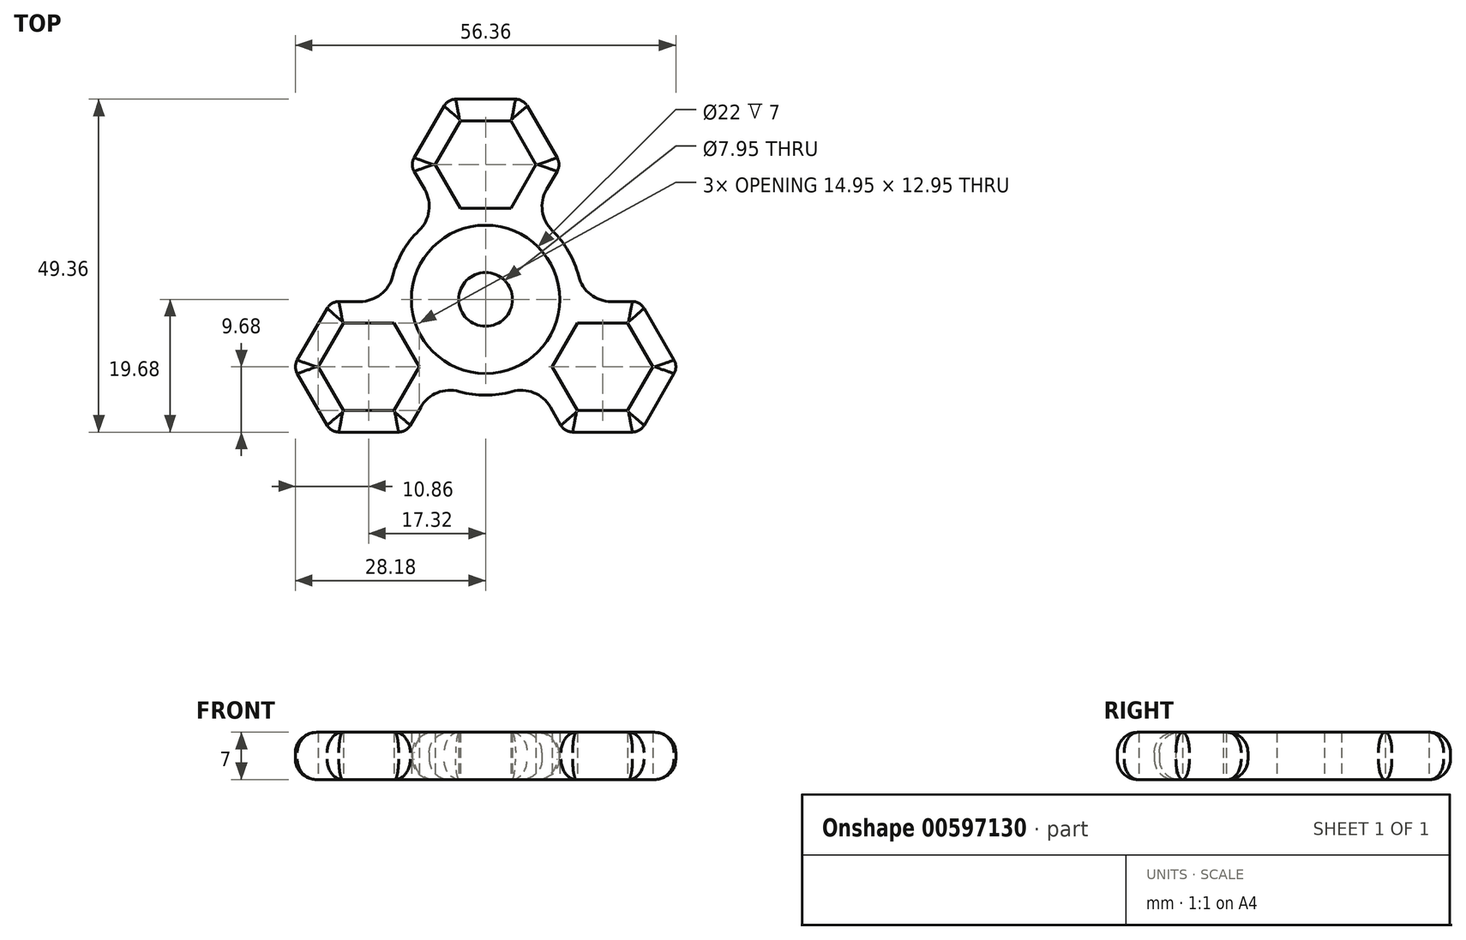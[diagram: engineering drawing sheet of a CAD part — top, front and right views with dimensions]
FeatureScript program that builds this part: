
annotation { "Feature Type Name" : "Feature", "Feature Type Description" : "" }
export const myFeature = defineFeature(function(context is Context, id is Id, definition is map)
    precondition{}
    {
        {
            var Q0;
            Q0=qCreatedBy(makeId("Top.planeOp"),FACE);
            var sketch = newSketch(context, id + "F0", { "sketchPlane" : qUnion([Q0])});
            skCircle(sketch, "E0", {"center": v(0, 0) * mm, "radius": 11 * mm});
            skCircle(sketch, "E1", {"center": v(0, 0) * mm, "radius": 3.98 * mm});
            skSolve(sketch);
        }
        {
            var Q0;
            Q0=qSketchRegion(id+"F0",true);
            extrude(context, id + "F1", {"entities" : qUnion([Q0]), "depth" : 7 * mm, "offsetDistance" : 25 * mm});
        }
        {
            var Q0;
            Q0=qCreatedBy(makeId("Top.planeOp"),FACE);
            var sketch = newSketch(context, id + "F2", { "sketchPlane" : qUnion([Q0])});
            skCircle(sketch, "E2.cCircle", {"center": v(0, 20) * mm, "radius": 6.47 * mm, "construction": true});
            skLineSegment(sketch, "E2.0", {"start": v(3.74, 26.48) * mm, "end": v(7.48, 20) * mm});
            skLineSegment(sketch, "E2.1", {"start": v(7.48, 20) * mm, "end": v(3.74, 13.53) * mm});
            skLineSegment(sketch, "E2.2", {"start": v(3.74, 13.53) * mm, "end": v(-3.74, 13.53) * mm});
            skLineSegment(sketch, "E2.3", {"start": v(-3.74, 13.52) * mm, "end": v(-7.48, 20) * mm});
            skLineSegment(sketch, "E2.4", {"start": v(-7.48, 20) * mm, "end": v(-3.74, 26.47) * mm});
            skLineSegment(sketch, "E2.5", {"start": v(-3.74, 26.47) * mm, "end": v(3.74, 26.47) * mm});
            skPoint(sketch, "E2.0.midPoint", {"position": v(5.6, 23.24) * mm});
            skLineSegment(sketch, "E3", {"start": v(0, 0) * mm, "end": v(0, 20) * mm, "construction": true});
            skLineSegment(sketch, "E4", {"start": v(0, 0) * mm, "end": v(-17.32, -10) * mm, "construction": true});
            skLineSegment(sketch, "E5", {"start": v(0, 0) * mm, "end": v(17.32, -10) * mm, "construction": true});
            skLineSegment(sketch, "E6.0", {"start": v(-4.43, 29.67) * mm, "end": v(4.43, 29.67) * mm});
            skLineSegment(sketch, "E6.1", {"start": v(10.6, 19) * mm, "end": v(9.03, 16.29) * mm});
            skLineSegment(sketch, "E6.3", {"start": v(6.16, 28.68) * mm, "end": v(10.6, 21) * mm});
            skLineSegment(sketch, "E6.4", {"start": v(-9.03, 16.29) * mm, "end": v(-10.6, 19) * mm});
            skLineSegment(sketch, "E6.5", {"start": v(-10.6, 21) * mm, "end": v(-6.16, 28.67) * mm});
            skCircle(sketch, "E7", {"center": v(0, 0) * mm, "radius": 11 * mm});
            skArc(sketch, "E8", {"start": v(-9.88, 10.2) * mm, "mid": v(-12.3, 7.1) * mm, "end": v(-13.77, 3.46) * mm});
            skLineSegment(sketch, "E9.1.0", {"start": v(-13.58, -16.47) * mm, "end": v(-21.06, -16.47) * mm});
            skLineSegment(sketch, "E9.1.1", {"start": v(-21.06, -16.48) * mm, "end": v(-24.8, -10) * mm});
            skLineSegment(sketch, "E9.1.2", {"start": v(-12.89, -19.67) * mm, "end": v(-21.75, -19.68) * mm});
            skLineSegment(sketch, "E9.1.3", {"start": v(-23.48, -18.68) * mm, "end": v(-27.91, -11) * mm});
            skLineSegment(sketch, "E9.1.4", {"start": v(-27.91, -9) * mm, "end": v(-23.48, -1.33) * mm});
            skLineSegment(sketch, "E9.1.5", {"start": v(-24.8, -10) * mm, "end": v(-21.06, -3.52) * mm});
            skLineSegment(sketch, "E9.1.6", {"start": v(-21.06, -3.53) * mm, "end": v(-13.58, -3.52) * mm});
            skLineSegment(sketch, "E9.1.7", {"start": v(-21.75, -0.33) * mm, "end": v(-18.62, -0.33) * mm});
            skLineSegment(sketch, "E9.1.8", {"start": v(-13.58, -3.52) * mm, "end": v(-9.84, -10) * mm});
            skLineSegment(sketch, "E9.1.9", {"start": v(-9.84, -10) * mm, "end": v(-13.58, -16.47) * mm});
            skLineSegment(sketch, "E9.1.10", {"start": v(-9.6, -15.96) * mm, "end": v(-11.16, -18.67) * mm});
            skLineSegment(sketch, "E9.2.0", {"start": v(21.06, -3.52) * mm, "end": v(24.8, -10) * mm});
            skLineSegment(sketch, "E9.2.1", {"start": v(24.8, -10) * mm, "end": v(21.06, -16.48) * mm});
            skLineSegment(sketch, "E9.2.2", {"start": v(23.48, -1.33) * mm, "end": v(27.91, -9) * mm});
            skLineSegment(sketch, "E9.2.3", {"start": v(27.91, -11) * mm, "end": v(23.48, -18.67) * mm});
            skLineSegment(sketch, "E9.2.4", {"start": v(21.75, -19.67) * mm, "end": v(12.89, -19.67) * mm});
            skLineSegment(sketch, "E9.2.5", {"start": v(21.06, -16.48) * mm, "end": v(13.58, -16.48) * mm});
            skLineSegment(sketch, "E9.2.6", {"start": v(13.58, -16.48) * mm, "end": v(9.84, -10) * mm});
            skLineSegment(sketch, "E9.2.7", {"start": v(11.16, -18.68) * mm, "end": v(9.6, -15.96) * mm});
            skLineSegment(sketch, "E9.2.8", {"start": v(9.84, -10) * mm, "end": v(13.58, -3.53) * mm});
            skLineSegment(sketch, "E9.2.9", {"start": v(13.58, -3.53) * mm, "end": v(21.06, -3.53) * mm});
            skLineSegment(sketch, "E9.2.10", {"start": v(18.62, -0.32) * mm, "end": v(21.75, -0.32) * mm});
            skArc(sketch, "E10.trimOffspring", {"start": v(-3.9, -13.66) * mm, "mid": v(0, -14.2) * mm, "end": v(3.9, -13.66) * mm});
            skArc(sketch, "E11.trimOffspring", {"start": v(13.77, 3.46) * mm, "mid": v(12.3, 7.1) * mm, "end": v(9.88, 10.2) * mm});
            skPoint(sketch, "E12.visualSharp", {"position": v(-6.82, 12.46) * mm});
            skArc(sketch, "E12.filletArc", {"start": v(-9.88, 10.2) * mm, "mid": v(-8.4, 13.1) * mm, "end": v(-9.03, 16.29) * mm});
            skPoint(sketch, "E13.visualSharp", {"position": v(6.82, 12.46) * mm});
            skArc(sketch, "E13.filletArc", {"start": v(9.03, 16.29) * mm, "mid": v(8.4, 13.1) * mm, "end": v(9.88, 10.2) * mm});
            skPoint(sketch, "E14.visualSharp", {"position": v(14.2, -0.32) * mm});
            skArc(sketch, "E14.filletArc", {"start": v(13.77, 3.46) * mm, "mid": v(15.55, 0.73) * mm, "end": v(18.62, -0.32) * mm});
            skPoint(sketch, "E15.visualSharp", {"position": v(7.38, -12.13) * mm});
            skArc(sketch, "E15.filletArc", {"start": v(9.6, -15.96) * mm, "mid": v(7.14, -13.83) * mm, "end": v(3.9, -13.66) * mm});
            skPoint(sketch, "E16.visualSharp", {"position": v(-7.38, -12.13) * mm});
            skArc(sketch, "E16.filletArc", {"start": v(-3.9, -13.66) * mm, "mid": v(-7.14, -13.83) * mm, "end": v(-9.6, -15.96) * mm});
            skPoint(sketch, "E17.visualSharp", {"position": v(-14.2, -0.32) * mm});
            skArc(sketch, "E17.filletArc", {"start": v(-18.62, -0.33) * mm, "mid": v(-15.55, 0.73) * mm, "end": v(-13.77, 3.46) * mm});
            skPoint(sketch, "E18.visualSharp", {"position": v(-5.59, 29.67) * mm});
            skArc(sketch, "E18.filletArc", {"start": v(-4.43, 29.67) * mm, "mid": v(-5.43, 29.4) * mm, "end": v(-6.16, 28.67) * mm});
            skPoint(sketch, "E19.visualSharp", {"position": v(5.59, 29.68) * mm});
            skArc(sketch, "E19.filletArc", {"start": v(6.16, 28.68) * mm, "mid": v(5.43, 29.4) * mm, "end": v(4.43, 29.68) * mm});
            skPoint(sketch, "E20.visualSharp", {"position": v(11.17, 20) * mm});
            skArc(sketch, "E20.filletArc", {"start": v(10.6, 19) * mm, "mid": v(10.86, 20) * mm, "end": v(10.6, 21) * mm});
            skPoint(sketch, "E21.visualSharp", {"position": v(-11.17, 20) * mm});
            skArc(sketch, "E21.filletArc", {"start": v(-10.6, 21) * mm, "mid": v(-10.86, 20) * mm, "end": v(-10.6, 19) * mm});
            skPoint(sketch, "E22.visualSharp", {"position": v(22.9, -0.32) * mm});
            skArc(sketch, "E22.filletArc", {"start": v(23.48, -1.32) * mm, "mid": v(22.75, -0.6) * mm, "end": v(21.75, -0.32) * mm});
            skPoint(sketch, "E23.visualSharp", {"position": v(28.5, -10) * mm});
            skArc(sketch, "E23.filletArc", {"start": v(27.91, -11) * mm, "mid": v(28.18, -10) * mm, "end": v(27.91, -9) * mm});
            skPoint(sketch, "E24.visualSharp", {"position": v(22.9, -19.67) * mm});
            skArc(sketch, "E24.filletArc", {"start": v(21.75, -19.67) * mm, "mid": v(22.75, -19.4) * mm, "end": v(23.48, -18.67) * mm});
            skPoint(sketch, "E25.visualSharp", {"position": v(11.73, -19.67) * mm});
            skArc(sketch, "E25.filletArc", {"start": v(11.16, -18.68) * mm, "mid": v(11.89, -19.4) * mm, "end": v(12.89, -19.67) * mm});
            skPoint(sketch, "E26.visualSharp", {"position": v(-11.73, -19.67) * mm});
            skArc(sketch, "E26.filletArc", {"start": v(-12.89, -19.67) * mm, "mid": v(-11.89, -19.4) * mm, "end": v(-11.16, -18.67) * mm});
            skPoint(sketch, "E27.visualSharp", {"position": v(-22.9, -19.68) * mm});
            skArc(sketch, "E27.filletArc", {"start": v(-23.48, -18.68) * mm, "mid": v(-22.75, -19.4) * mm, "end": v(-21.75, -19.68) * mm});
            skPoint(sketch, "E28.visualSharp", {"position": v(-28.5, -10) * mm});
            skArc(sketch, "E28.filletArc", {"start": v(-27.91, -9) * mm, "mid": v(-28.18, -10) * mm, "end": v(-27.91, -11) * mm});
            skPoint(sketch, "E29.visualSharp", {"position": v(-22.9, -0.33) * mm});
            skArc(sketch, "E29.filletArc", {"start": v(-21.75, -0.33) * mm, "mid": v(-22.75, -0.6) * mm, "end": v(-23.48, -1.33) * mm});
            skSolve(sketch);
        }
        {
            var Q0;
            Q0=qSketchRegion(id+"F2",true);
            extrude(context, id + "F3", {"entities" : qUnion([Q0]), "depth" : 7 * mm, "offsetDistance" : 25 * mm});
        }
        {
            var Q0;
            Q0=makeQuery(id+"F3.opExtrude","CAP_EDGE",EDGE,{"disambiguationData":[OSD([sQuery(id+"F2.wireOp",EDGE,"E10.trimOffspring")])],"isStart":false});
            var Q1;
            Q1=makeQuery(id+"F3.opExtrude","CAP_EDGE",EDGE,{"disambiguationData":[OSD([sQuery(id+"F2.wireOp",EDGE,"E10.trimOffspring")])],"isStart":true});
            fillet(context, id + "F4", {"entities" : qUnion([Q0, Q1]), "radius" : 3 * mm, "tangentPropagation" : true, "allowEdgeOverflow" : false});
        }
    });
